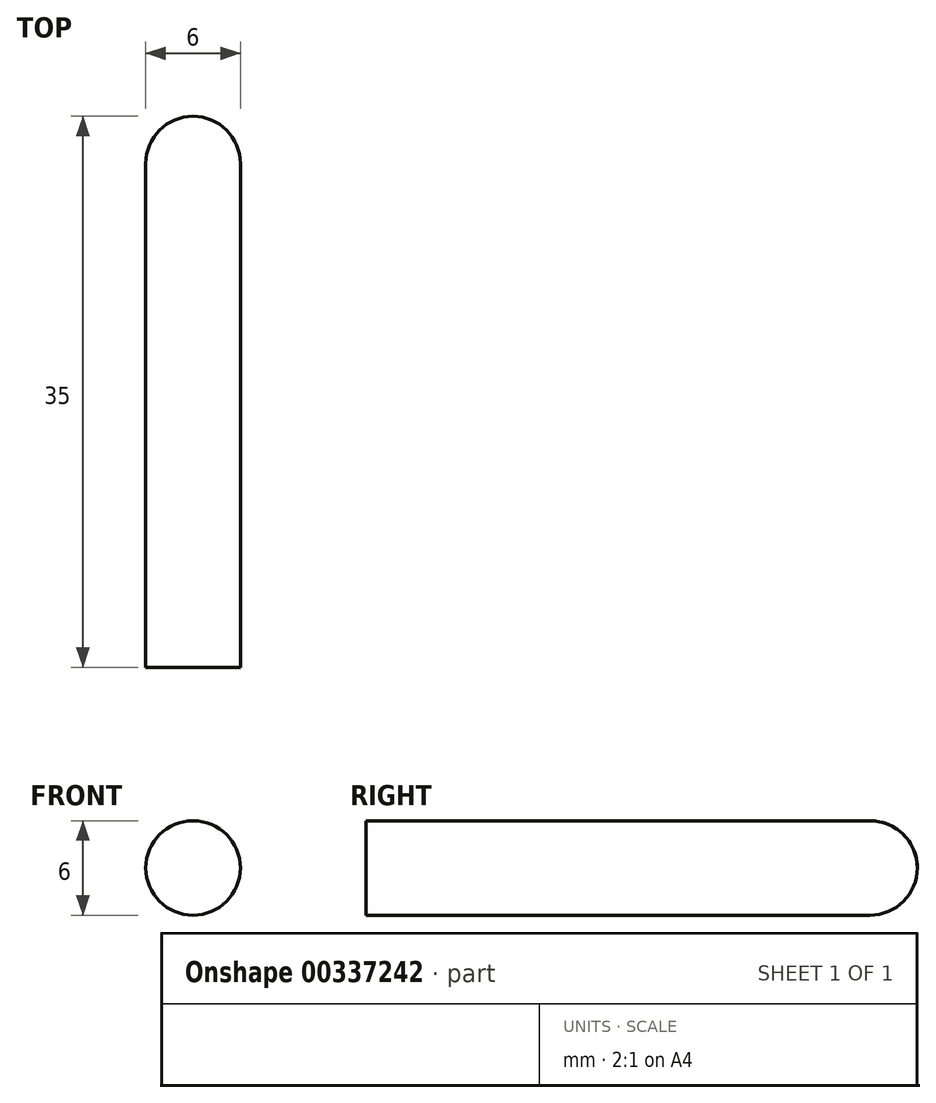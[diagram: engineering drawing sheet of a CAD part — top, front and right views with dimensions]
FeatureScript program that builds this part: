
annotation { "Feature Type Name" : "Feature", "Feature Type Description" : "" }
export const myFeature = defineFeature(function(context is Context, id is Id, definition is map)
    precondition{}
    {
        {
            var Q0;
            Q0=qCreatedBy(makeId("Top.planeOp"),FACE);
            var sketch = newSketch(context, id + "F0", { "sketchPlane" : qUnion([Q0])});
            skLineSegment(sketch, "E0.bottom", {"start": v(0, 0) * mm, "end": v(6, 0) * mm});
            skLineSegment(sketch, "E0.top", {"start": v(0, 35) * mm, "end": v(6, 35) * mm});
            skLineSegment(sketch, "E0.left", {"start": v(0, 0) * mm, "end": v(0, 35) * mm});
            skLineSegment(sketch, "E0.right", {"start": v(6, 0) * mm, "end": v(6, 35) * mm});
            skLineSegment(sketch, "E1", {"start": v(3, 56.08) * mm, "end": v(3, -36.07) * mm});
            skPoint(sketch, "E1.startSnap0", {"position": v(3, 35) * mm});
            skSolve(sketch);
        }
        {
            var Q0;
            {var subQ0=sQuery(id+"F0.wireOp",EDGE,"E0.right");Q0=makeQuery(id+"F0.imprint","IMPRINT",FACE,{"disambiguationData":[TD([[makeQuery(id+"F0.imprint","IMPRINT",EDGE,{"derivedFrom":subQ0}),1.0]])]});}
            var Q1;
            Q1=sQuery(id+"F0.wireOp",EDGE,"E1");
            revolve(context, id + "F1", {"entities" : qUnion([Q0]), "axis" : qUnion([Q1]), "revolveType" : RevolveType.FULL});
        }
        {
            var Q0;
            Q0=makeQuery(id+"F1.opRevolve","SWEPT_EDGE",EDGE,{"disambiguationData":[OSD([sQuery(id+"F0.wireOp",EDGE,"E0.top"),sQuery(id+"F0.wireOp",EDGE,"E0.right")])]});
            fillet(context, id + "F2", {"entities" : qUnion([Q0]), "radius" : 3 * mm, "tangentPropagation" : true, "allowEdgeOverflow" : false});
        }
    });
